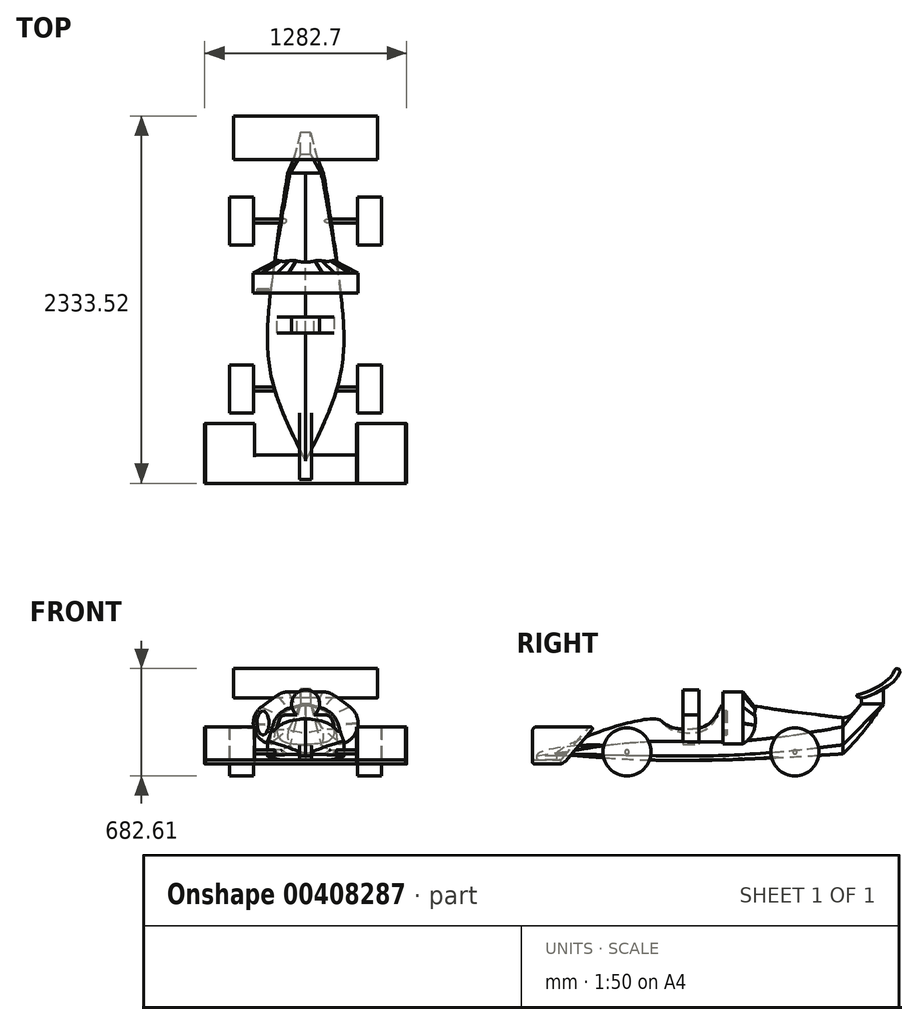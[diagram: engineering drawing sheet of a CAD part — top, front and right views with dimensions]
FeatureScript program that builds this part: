
annotation { "Feature Type Name" : "Feature", "Feature Type Description" : "" }
export const myFeature = defineFeature(function(context is Context, id is Id, definition is map)
    precondition{}
    {
        {
            var Q0;
            Q0=qCreatedBy(makeId("Right.planeOp"),FACE);
            var sketch = newSketch(context, id + "F0", { "sketchPlane" : qUnion([Q0])});
            skLineSegment(sketch, "E0", {"start": v(0, 0) * mm, "end": v(1066.8, 0) * mm, "construction": true});
            skLineSegment(sketch, "E1", {"start": v(0, 0) * mm, "end": v(-1066.8, 0) * mm, "construction": true});
            skLineSegment(sketch, "E2", {"start": v(0, 0) * mm, "end": v(0, 762) * mm, "construction": true});
            skSolve(sketch);
        }
        {
            var Q0;
            Q0=qCreatedBy(makeId("Front.planeOp"),FACE);
            cPlane(context, id + "F1", {"entities" : qUnion([Q0]), "cplaneType" : CPlaneType.OFFSET, "offset" : 1066.8 * mm, "width" : 152.4 * mm, "height" : 152.4 * mm});
        }
        {
            var Q0;
            Q0=qCreatedBy(makeId("Front.planeOp"),FACE);
            cPlane(context, id + "F2", {"entities" : qUnion([Q0]), "cplaneType" : CPlaneType.OFFSET, "offset" : 762 * mm, "oppositeDirection" : true, "width" : 152.4 * mm, "height" : 152.4 * mm});
        }
        {
            var Q0;
            Q0=qCreatedBy(id+"F1.planeOp",FACE);
            var sketch = newSketch(context, id + "F3", { "sketchPlane" : qUnion([Q0])});
            skLineSegment(sketch, "E3", {"start": v(0, 0) * mm, "end": v(0, 88.9) * mm, "construction": true});
            skPoint(sketch, "E4", {"position": v(0, 88.9) * mm});
            skSolve(sketch);
        }
        {
            var Q0;
            Q0=qCreatedBy(makeId("Front.planeOp"),FACE);
            cPlane(context, id + "F4", {"entities" : qUnion([Q0]), "cplaneType" : CPlaneType.OFFSET, "offset" : 508 * mm, "width" : 152.4 * mm, "height" : 152.4 * mm});
        }
        {
            var Q0;
            Q0=qCreatedBy(id+"F4.planeOp",FACE);
            var sketch = newSketch(context, id + "F5", { "sketchPlane" : qUnion([Q0])});
            skLineSegment(sketch, "E5", {"start": v(0, 0) * mm, "end": v(0, 304.8) * mm, "construction": true});
            skFitSpline(sketch, "E6", {"points": [v(0, 304.8) * mm, v(132.6, 270.36) * mm, v(222.86, 165.59) * mm], "startDerivative": vector(287.19, -34.12) * mm, "endDerivative": vector(158.63, -244.14) * mm});
            skLineSegment(sketch, "E7", {"start": v(222.86, 165.59) * mm, "end": v(222.86, 78.54) * mm});
            skFitSpline(sketch, "E8", {"points": [v(222.86, 78.54) * mm, v(150.32, 59.2) * mm, v(0, 51.14) * mm], "startDerivative": vector(-158.44, -53.56) * mm, "endDerivative": vector(-280.28, -4.09) * mm});
            skFitSpline(sketch, "E9.MirrorCS", {"points": [v(0, 304.8) * mm, v(-132.6, 270.36) * mm, v(-222.86, 165.59) * mm], "startDerivative": vector(-287.19, -34.12) * mm, "endDerivative": vector(-158.63, -244.14) * mm});
            skLineSegment(sketch, "E10.MirrorCS", {"start": v(-222.86, 165.59) * mm, "end": v(-222.86, 78.54) * mm});
            skFitSpline(sketch, "E11.MirrorCS", {"points": [v(-222.86, 78.54) * mm, v(-150.32, 59.2) * mm, v(0, 51.14) * mm], "startDerivative": vector(158.44, -53.56) * mm, "endDerivative": vector(280.28, -4.09) * mm});
            skSolve(sketch);
        }
        {
            var Q0;
            Q0=qCreatedBy(makeId("Front.planeOp"),FACE);
            var sketch = newSketch(context, id + "F6", { "sketchPlane" : qUnion([Q0])});
            skFitSpline(sketch, "E12.0", {"points": [v(-222.86, 78.54) * mm, v(-201, 71.16) * mm, v(-148.18, 53.3) * mm, v(-54.76, 51.94) * mm, v(0, 51.14) * mm]});
            skPoint(sketch, "E13.0", {"position": v(112.83, 54.96) * mm});
            skLineSegment(sketch, "E14.0", {"start": v(222.86, 165.59) * mm, "end": v(222.86, 78.54) * mm});
            skLineSegment(sketch, "E15.0", {"start": v(-222.86, 165.59) * mm, "end": v(-222.86, 78.54) * mm});
            skFitSpline(sketch, "E16", {"points": [v(-222.86, 165.59) * mm, v(-211.16, 257.47) * mm, v(-154.74, 352.57) * mm, v(-25.8, 402.54) * mm, v(0, 404.15) * mm], "startDerivative": vector(24.48, 349.4) * mm, "endDerivative": vector(143.3, -4.49) * mm});
            skFitSpline(sketch, "E17.MirrorCS", {"points": [v(222.86, 165.59) * mm, v(211.16, 257.47) * mm, v(154.74, 352.57) * mm, v(25.8, 402.54) * mm, v(0, 404.15) * mm], "startDerivative": vector(-24.48, 349.4) * mm, "endDerivative": vector(-143.3, -4.49) * mm});
            skFitSpline(sketch, "E18.MirrorCS", {"points": [v(222.86, 78.54) * mm, v(201, 71.16) * mm, v(148.18, 53.3) * mm, v(54.76, 51.94) * mm, v(0, 51.14) * mm]});
            skSolve(sketch);
        }
        {
            var Q0;
            Q0=qCreatedBy(id+"F2.planeOp",FACE);
            var sketch = newSketch(context, id + "F7", { "sketchPlane" : qUnion([Q0])});
            skLineSegment(sketch, "E19", {"start": v(0, 0) * mm, "end": v(0, 203.2) * mm, "construction": true});
            skCircle(sketch, "E20", {"center": v(0, 203.2) * mm, "radius": 114.3 * mm});
            skSolve(sketch);
        }
        {
            var Q0;
            Q0=qCreatedBy(makeId("Right.planeOp"),FACE);
            var sketch = newSketch(context, id + "F8", { "sketchPlane" : qUnion([Q0])});
            skPoint(sketch, "E21.0", {"position": v(-1066.8, 88.9) * mm});
            skFitSpline(sketch, "E22.0", {"points": [v(-508, 304.8) * mm, v(-508, 299.13) * mm, v(-508, 287.76) * mm, v(-508, 206.38) * mm, v(-508, 165.59) * mm]});
            skPoint(sketch, "E23.0", {"position": v(-508, 51.14) * mm});
            skPoint(sketch, "E24.0", {"position": v(0, 404.15) * mm});
            skPoint(sketch, "E25.0", {"position": v(0, 54.96) * mm});
            skLineSegment(sketch, "E26.0", {"start": v(762, 88.9) * mm, "end": v(762, 317.5) * mm});
            skFitSpline(sketch, "E27", {"points": [v(-1066.8, 88.9) * mm, v(-974.26, 150.13) * mm, v(-703.34, 256.94) * mm, v(-508, 304.8) * mm, v(-401.17, 304.8) * mm, v(-336.04, 249.12) * mm, v(-91.17, 254.33) * mm, v(0, 404.15) * mm, v(138.06, 404.15) * mm, v(401.17, 361.13) * mm, v(440.24, 355.92) * mm, v(762, 317.5) * mm], "startDerivative": vector(1027.27, 794.62) * mm, "endDerivative": vector(3267.51, -388.12) * mm});
            skFitSpline(sketch, "E28", {"points": [v(-1066.8, 88.9) * mm, v(-807.54, 51.14) * mm, v(-508, 51.14) * mm, v(0, 54.96) * mm, v(500.16, 54.96) * mm, v(762, 88.9) * mm], "startDerivative": vector(1511.97, -275.41) * mm, "endDerivative": vector(1399.72, 243.02) * mm});
            skSolve(sketch);
        }
        {
            var Q0;
            Q0=sQuery(id+"F8.wireOp",VERTEX,"E21.0");
            var Q1;
            Q1=makeQuery(id+"F5.imprint","IMPRINT",FACE,{"disambiguationData":[TD([[makeQuery(id+"F5.imprint","IMPRINT",EDGE,{"derivedFrom":sQuery(id+"F5.wireOp",EDGE,"E6")}),-1.0]])]});
            var Q2;
            Q2=makeQuery(id+"F6.imprint","IMPRINT",FACE,{"disambiguationData":[TD([[makeQuery(id+"F6.imprint","IMPRINT",EDGE,{"derivedFrom":sQuery(id+"F6.wireOp",EDGE,"E12.0")}),1.0]])]});
            var Q3;
            Q3=makeQuery(id+"F7.imprint","IMPRINT",FACE,{"disambiguationData":[TD([[makeQuery(id+"F7.imprint","IMPRINT",EDGE,{"derivedFrom":sQuery(id+"F7.wireOp",EDGE,"E20")}),1.0]])]});
            var Q4;
            Q4=sQuery(id+"F8.wireOp",EDGE,"E27");
            loft(context, id + "F9", {"addGuides" : true, "sheetProfilesArray" : [{ "sheetProfileEntities" : qUnion([Q0]) }, { "sheetProfileEntities" : qUnion([Q1]) }, { "sheetProfileEntities" : qUnion([Q2]) }, { "sheetProfileEntities" : qUnion([Q3]) }], "guidesArray" : [{ "guideEntities" : qUnion([Q4]), "guideDerivativeType" : LoftGuideDerivativeType.DEFAULT, "guideDerivativeMagnitude" : 1 }]});
        }
        {
            var Q0;
            Q0=qCreatedBy(makeId("Right.planeOp"),FACE);
            cPlane(context, id + "F10", {"entities" : qUnion([Q0]), "cplaneType" : CPlaneType.OFFSET, "offset" : 330.2 * mm, "width" : 152.4 * mm, "height" : 152.4 * mm});
        }
        {
            var Q0;
            Q0=qCreatedBy(id+"F10.planeOp",FACE);
            var sketch = newSketch(context, id + "F11", { "sketchPlane" : qUnion([Q0])});
            skLineSegment(sketch, "E29", {"start": v(0, 0) * mm, "end": v(-609.6, 0) * mm, "construction": true});
            skLineSegment(sketch, "E30", {"start": v(-609.6, 0) * mm, "end": v(-609.6, 101.6) * mm, "construction": true});
            skLineSegment(sketch, "E31", {"start": v(0, 0) * mm, "end": v(457.2, 0) * mm, "construction": true});
            skLineSegment(sketch, "E32", {"start": v(457.2, 0) * mm, "end": v(457.2, 101.6) * mm, "construction": true});
            skCircle(sketch, "E33", {"center": v(-609.6, 101.6) * mm, "radius": 152.4 * mm});
            skCircle(sketch, "E34", {"center": v(457.2, 101.6) * mm, "radius": 152.4 * mm});
            skSolve(sketch);
        }
        {
            var Q0;
            Q0=makeQuery(id+"F11.imprint","IMPRINT",FACE,{"disambiguationData":[TD([[makeQuery(id+"F11.imprint","IMPRINT",EDGE,{"derivedFrom":sQuery(id+"F11.wireOp",EDGE,"E33")}),1.0]])]});
            var Q1;
            Q1=makeQuery(id+"F11.imprint","IMPRINT",FACE,{"disambiguationData":[TD([[makeQuery(id+"F11.imprint","IMPRINT",EDGE,{"derivedFrom":sQuery(id+"F11.wireOp",EDGE,"E34")}),1.0]])]});
            extrude(context, id + "F12", {"entities" : qUnion([Q0, Q1]), "depth" : 152.4 * mm});
        }
        {
            var Q0;
            Q0=makeQuery(id+"F12.opExtrude","CAP_FACE",FACE,{"disambiguationData":[OSD([sQuery(id+"F11.wireOp",EDGE,"E33")])],"isStart":true});
            var sketch = newSketch(context, id + "F13", { "sketchPlane" : qUnion([Q0])});
            skCircle(sketch, "E35", {"center": v(609.6, 101.6) * mm, "radius": 12.7 * mm});
            skSolve(sketch);
        }
        {
            var Q0;
            Q0=makeQuery(id+"F13.imprint","IMPRINT",FACE,{"disambiguationData":[TD([[makeQuery(id+"F13.imprint","IMPRINT",EDGE,{"derivedFrom":sQuery(id+"F13.wireOp",EDGE,"E35")}),1.0]])]});
            extrude(context, id + "F14", {"entities" : qUnion([Q0]), "endBound" : BoundingType.UP_TO_NEXT, "depth" : 25.4 * mm});
        }
        {
            var Q0;
            Q0=makeQuery(id+"F12.opExtrude","CAP_FACE",FACE,{"disambiguationData":[OSD([sQuery(id+"F11.wireOp",EDGE,"E34")])],"isStart":true});
            var sketch = newSketch(context, id + "F15", { "sketchPlane" : qUnion([Q0])});
            skCircle(sketch, "E36", {"center": v(-457.2, 101.6) * mm, "radius": 12.7 * mm});
            skSolve(sketch);
        }
        {
            var Q0;
            Q0=makeQuery(id+"F15.imprint","IMPRINT",FACE,{"disambiguationData":[TD([[makeQuery(id+"F15.imprint","IMPRINT",EDGE,{"derivedFrom":sQuery(id+"F15.wireOp",EDGE,"E36")}),1.0]])]});
            extrude(context, id + "F16", {"entities" : qUnion([Q0]), "endBound" : BoundingType.UP_TO_NEXT, "depth" : 25.4 * mm});
        }
        {
            var Q0;
            Q0=qCreatedBy(makeId("Right.planeOp"),FACE);
            var sketch = newSketch(context, id + "F17", { "sketchPlane" : qUnion([Q0])});
            skFitSpline(sketch, "E37", {"points": [v(873.59, 445.04) * mm, v(963.54, 473.71) * mm, v(1092.94, 556.82) * mm, v(1122.28, 622.83) * mm, v(1097.34, 630.16) * mm, v(1081.2, 597.9) * mm, v(1017, 537) * mm, v(949.39, 498.44) * mm, v(889.96, 474.72) * mm, v(847.68, 458.19) * mm, v(873.59, 445.04) * mm]});
            skSolve(sketch);
        }
        {
            var Q0;
            Q0=makeQuery(id+"F17.imprint","IMPRINT",FACE,{"disambiguationData":[TD([[makeQuery(id+"F17.imprint","IMPRINT",EDGE,{"derivedFrom":sQuery(id+"F17.wireOp",EDGE,"E37")}),1.0]])]});
            extrude(context, id + "F18", {"entities" : qUnion([Q0]), "endBound" : BoundingType.SYMMETRIC, "depth" : 914.4 * mm});
        }
        {
            var Q0;
            Q0=makeQuery(id+"F18.opExtrude","CAP_FACE",FACE,{"disambiguationData":[OSD([sQuery(id+"F17.wireOp",EDGE,"E37")])],"isStart":false});
            cPlane(context, id + "F19", {"entities" : qUnion([Q0]), "cplaneType" : CPlaneType.OFFSET, "offset" : 177.8 * mm, "width" : 152.4 * mm, "height" : 152.4 * mm});
        }
        {
            var Q0;
            Q0=qCreatedBy(id+"F19.planeOp",FACE);
            var sketch = newSketch(context, id + "F20", { "sketchPlane" : qUnion([Q0])});
            skArc(sketch, "E38", {"start": v(-1196.29, 50.01) * mm, "mid": v(-1208.99, 37.31) * mm, "end": v(-1196.29, 24.61) * mm});
            skLineSegment(sketch, "E39", {"start": v(-1196.29, 50.01) * mm, "end": v(-1039.81, 50.01) * mm});
            skLineSegment(sketch, "E40", {"start": v(-1020.5, 58.9) * mm, "end": v(-851.65, 256.45) * mm});
            skPoint(sketch, "E41.visualSharp", {"position": v(-1028.11, 50.01) * mm});
            skArc(sketch, "E41.filletArc", {"start": v(-1039.81, 50.01) * mm, "mid": v(-1029.18, 52.34) * mm, "end": v(-1020.5, 58.9) * mm});
            skLineSegment(sketch, "E42.0", {"start": v(-1001.2, 42.4) * mm, "end": v(-832.34, 239.94) * mm});
            skArc(sketch, "E42.1", {"start": v(-1039.81, 24.61) * mm, "mid": v(-1018.56, 29.28) * mm, "end": v(-1001.2, 42.4) * mm});
            skLineSegment(sketch, "E42.2", {"start": v(-1196.29, 24.61) * mm, "end": v(-1039.81, 24.61) * mm});
            skArc(sketch, "E43", {"start": v(-851.65, 256.45) * mm, "mid": v(-833.74, 257.85) * mm, "end": v(-832.34, 239.94) * mm});
            skSolve(sketch);
        }
        {
            var Q0;
            Q0 = qSketchRegion(id + "F20", true);
            extrude(context, id + "F21", {"entities" : qUnion([Q0]), "oppositeDirection" : true, "depth" : 304.8 * mm});
        }
        {
            var Q0;
            Q0=makeQuery(id+"F21.opExtrude","CAP_FACE",FACE,{"disambiguationData":[OSD([sQuery(id+"F20.wireOp",EDGE,"E38"),sQuery(id+"F20.wireOp",EDGE,"E39"),sQuery(id+"F20.wireOp",EDGE,"E40"),sQuery(id+"F20.wireOp",EDGE,"E41.filletArc"),sQuery(id+"F20.wireOp",EDGE,"E42.0"),sQuery(id+"F20.wireOp",EDGE,"E42.1"),sQuery(id+"F20.wireOp",EDGE,"E42.2"),sQuery(id+"F20.wireOp",EDGE,"E43")])],"isStart":false});
            var sketch = newSketch(context, id + "F22", { "sketchPlane" : qUnion([Q0])});
            skArc(sketch, "E44.0", {"start": v(1196.29, 50.01) * mm, "mid": v(1208.99, 37.31) * mm, "end": v(1196.29, 24.61) * mm});
            skLineSegment(sketch, "E45.0", {"start": v(1196.29, 50.01) * mm, "end": v(1039.81, 50.01) * mm});
            skLineSegment(sketch, "E46.0", {"start": v(1196.29, 24.61) * mm, "end": v(1039.81, 24.61) * mm});
            skArc(sketch, "E47", {"start": v(1039.81, 50.01) * mm, "mid": v(1027.11, 37.31) * mm, "end": v(1039.81, 24.61) * mm});
            skSolve(sketch);
        }
        {
            var Q0;
            Q0=makeQuery(id+"F22.imprint","IMPRINT",FACE,{"disambiguationData":[TD([[makeQuery(id+"F22.imprint","IMPRINT",EDGE,{"derivedFrom":sQuery(id+"F22.wireOp",EDGE,"E44.0")}),-1.0]])]});
            var Q1;
            Q1=qCreatedBy(makeId("Right.planeOp"),FACE);
            extrude(context, id + "F23", {"entities" : qUnion([Q0]), "operationType" : NewBodyOperationType.ADD, "endBound" : BoundingType.UP_TO_SURFACE, "endBoundEntityFace" : qUnion([Q1]), "depth" : 25.4 * mm});
        }
        {
            var Q0;
            Q0=makeQuery(id+"F21.opExtrude","SWEPT_BODY",BODY,{"disambiguationData":[OSD([sQuery(id+"F20.wireOp",EDGE,"E38"),sQuery(id+"F20.wireOp",EDGE,"E39"),sQuery(id+"F20.wireOp",EDGE,"E40"),sQuery(id+"F20.wireOp",EDGE,"E41.filletArc"),sQuery(id+"F20.wireOp",EDGE,"E42.0"),sQuery(id+"F20.wireOp",EDGE,"E42.1"),sQuery(id+"F20.wireOp",EDGE,"E42.2"),sQuery(id+"F20.wireOp",EDGE,"E43")])]});
            var Q1;
            Q1=qCreatedBy(makeId("Right.planeOp"),FACE);
            mirror(context, id + "F24", {"operationType" : NewBodyOperationType.ADD, "entities" : qUnion([Q0]), "mirrorPlane" : qUnion([Q1])});
        }
        {
            var Q0;
            Q0=makeQuery(id+"F21.opExtrude","CAP_FACE",FACE,{"disambiguationData":[OSD([sQuery(id+"F20.wireOp",EDGE,"E38"),sQuery(id+"F20.wireOp",EDGE,"E39"),sQuery(id+"F20.wireOp",EDGE,"E40"),sQuery(id+"F20.wireOp",EDGE,"E41.filletArc"),sQuery(id+"F20.wireOp",EDGE,"E42.0"),sQuery(id+"F20.wireOp",EDGE,"E42.1"),sQuery(id+"F20.wireOp",EDGE,"E42.2"),sQuery(id+"F20.wireOp",EDGE,"E43")])],"isStart":true});
            var sketch = newSketch(context, id + "F25", { "sketchPlane" : qUnion([Q0])});
            skArc(sketch, "E48.0", {"start": v(-851.65, 256.45) * mm, "mid": v(-833.74, 257.85) * mm, "end": v(-832.34, 239.94) * mm, "construction": true});
            skArc(sketch, "E49.0", {"start": v(-1196.29, 50.01) * mm, "mid": v(-1208.99, 37.31) * mm, "end": v(-1196.29, 24.61) * mm, "construction": true});
            skLineSegment(sketch, "E50", {"start": v(-842, 248.2) * mm, "end": v(-842, 260.9) * mm, "construction": true});
            skLineSegment(sketch, "E51", {"start": v(-842, 260.9) * mm, "end": v(-1183.59, 260.9) * mm});
            skPoint(sketch, "E51.endSnap0", {"position": v(-1208.99, 37.31) * mm});
            skLineSegment(sketch, "E52", {"start": v(-1208.99, 235.5) * mm, "end": v(-1208.99, 37.31) * mm});
            skPoint(sketch, "E53.visualSharp", {"position": v(-1208.99, 260.9) * mm});
            skArc(sketch, "E53.filletArc", {"start": v(-1183.59, 260.9) * mm, "mid": v(-1201.55, 253.45) * mm, "end": v(-1208.99, 235.5) * mm});
            skLineSegment(sketch, "E54.0", {"start": v(-1196.29, 24.61) * mm, "end": v(-1039.81, 24.61) * mm});
            skArc(sketch, "E55.0", {"start": v(-1039.81, 24.61) * mm, "mid": v(-1018.56, 29.28) * mm, "end": v(-1001.2, 42.4) * mm});
            skLineSegment(sketch, "E56.0", {"start": v(-1001.2, 42.4) * mm, "end": v(-832.34, 239.94) * mm});
            skSolve(sketch);
        }
        {
            var Q0;
            {var subQ2=sQuery(id+"F25.wireOp",EDGE,"E54.0");Q0=makeQuery(id+"F25.imprint","IMPRINT",FACE,{"disambiguationData":[TD([[makeQuery(id+"F25.imprint","IMPRINT",EDGE,{"derivedFrom":subQ2}),1.0]])]});}
            var Q1;
            {var subQ4=sQuery(id+"F25.wireOp",EDGE,"E51");Q1=makeQuery(id+"F25.imprint","IMPRINT",FACE,{"disambiguationData":[TD([[makeQuery(id+"F25.imprint","IMPRINT",EDGE,{"derivedFrom":subQ4}),1.0]])]});}
            extrude(context, id + "F26", {"entities" : qUnion([Q0, Q1]), "operationType" : NewBodyOperationType.ADD, "depth" : 6.35 * mm});
        }
        {
            var Q0;
            Q0=makeQuery(id+"F24.opPattern","COPY",FACE,{"derivedFrom":makeQuery(id+"F21.opExtrude","CAP_FACE",FACE,{"disambiguationData":[OSD([sQuery(id+"F20.wireOp",EDGE,"E38"),sQuery(id+"F20.wireOp",EDGE,"E39"),sQuery(id+"F20.wireOp",EDGE,"E40"),sQuery(id+"F20.wireOp",EDGE,"E41.filletArc"),sQuery(id+"F20.wireOp",EDGE,"E42.0"),sQuery(id+"F20.wireOp",EDGE,"E42.1"),sQuery(id+"F20.wireOp",EDGE,"E42.2"),sQuery(id+"F20.wireOp",EDGE,"E43")])],"isStart":true}),"instanceName":"1"});
            var sketch = newSketch(context, id + "F27", { "sketchPlane" : qUnion([Q0])});
            skArc(sketch, "E57.0.0", {"start": v(842, 260.9) * mm, "mid": v(847.31, 259.73) * mm, "end": v(851.65, 256.45) * mm});
            skLineSegment(sketch, "E57.0.1", {"start": v(851.65, 256.45) * mm, "end": v(1020.5, 58.9) * mm});
            skArc(sketch, "E57.0.2", {"start": v(1020.5, 58.9) * mm, "mid": v(1029.18, 52.34) * mm, "end": v(1039.81, 50.01) * mm});
            skLineSegment(sketch, "E57.0.3", {"start": v(1039.81, 50.01) * mm, "end": v(1196.29, 50.01) * mm});
            skArc(sketch, "E57.0.4", {"start": v(1196.29, 50.01) * mm, "mid": v(1205.27, 46.3) * mm, "end": v(1208.99, 37.31) * mm});
            skLineSegment(sketch, "E57.0.5", {"start": v(1208.99, 37.31) * mm, "end": v(1208.99, 235.5) * mm});
            skArc(sketch, "E57.0.6", {"start": v(1208.99, 235.5) * mm, "mid": v(1201.55, 253.45) * mm, "end": v(1183.59, 260.9) * mm});
            skLineSegment(sketch, "E57.0.7", {"start": v(1183.59, 260.9) * mm, "end": v(842, 260.9) * mm});
            skSolve(sketch);
        }
        {
            var Q0;
            Q0=makeQuery(id+"F27.imprint","IMPRINT",FACE,{"disambiguationData":[TD([[makeQuery(id+"F27.imprint","IMPRINT",EDGE,{"derivedFrom":sQuery(id+"F27.wireOp",EDGE,"E57.0.0")}),-1.0]])]});
            var Q1;
            {var subQ2=sQuery(id+"F27.wireOp",EDGE,"E57.0.0");Q1=makeQuery(id+"F27.imprint","IMPRINT",FACE,{"disambiguationData":[TD([[makeQuery(id+"F27.imprint","IMPRINT",EDGE,{"derivedFrom":subQ2}),1.0]])]});}
            extrude(context, id + "F28", {"entities" : qUnion([Q0, Q1]), "operationType" : NewBodyOperationType.ADD, "depth" : 6.35 * mm});
        }
        {
            var Q0;
            Q0=makeQuery(id+"F21.opExtrude","CAP_FACE",FACE,{"disambiguationData":[OSD([sQuery(id+"F20.wireOp",EDGE,"E38"),sQuery(id+"F20.wireOp",EDGE,"E39"),sQuery(id+"F20.wireOp",EDGE,"E40"),sQuery(id+"F20.wireOp",EDGE,"E41.filletArc"),sQuery(id+"F20.wireOp",EDGE,"E42.0"),sQuery(id+"F20.wireOp",EDGE,"E42.1"),sQuery(id+"F20.wireOp",EDGE,"E42.2"),sQuery(id+"F20.wireOp",EDGE,"E43")])],"isStart":false});
            var sketch = newSketch(context, id + "F29", { "sketchPlane" : qUnion([Q0])});
            skArc(sketch, "E58.0.0", {"start": v(842, 260.9) * mm, "mid": v(847.31, 259.73) * mm, "end": v(851.65, 256.45) * mm});
            skLineSegment(sketch, "E58.0.1", {"start": v(851.65, 256.45) * mm, "end": v(1020.5, 58.9) * mm});
            skArc(sketch, "E58.0.2", {"start": v(1020.5, 58.9) * mm, "mid": v(1029.18, 52.34) * mm, "end": v(1039.81, 50.01) * mm});
            skLineSegment(sketch, "E58.0.3", {"start": v(1039.81, 50.01) * mm, "end": v(1196.29, 50.01) * mm});
            skArc(sketch, "E58.0.4", {"start": v(1196.29, 50.01) * mm, "mid": v(1205.27, 46.3) * mm, "end": v(1208.99, 37.31) * mm});
            skLineSegment(sketch, "E58.0.5", {"start": v(1208.99, 37.31) * mm, "end": v(1208.99, 235.5) * mm});
            skArc(sketch, "E58.0.6", {"start": v(1208.99, 235.5) * mm, "mid": v(1201.55, 253.45) * mm, "end": v(1183.59, 260.9) * mm});
            skLineSegment(sketch, "E58.0.7", {"start": v(1183.59, 260.9) * mm, "end": v(842, 260.9) * mm});
            skSolve(sketch);
        }
        {
            var Q0;
            Q0=makeQuery(id+"F29.imprint","IMPRINT",FACE,{"disambiguationData":[TD([[makeQuery(id+"F29.imprint","IMPRINT",EDGE,{"derivedFrom":sQuery(id+"F29.wireOp",EDGE,"E58.0.0")}),-1.0]])]});
            var Q1;
            {var subQ1=sQuery(id+"F29.wireOp",EDGE,"E58.0.0");Q1=makeQuery(id+"F29.imprint","IMPRINT",FACE,{"disambiguationData":[TD([[makeQuery(id+"F29.imprint","IMPRINT",EDGE,{"derivedFrom":subQ1}),1.0]])]});}
            extrude(context, id + "F30", {"entities" : qUnion([Q0, Q1]), "operationType" : NewBodyOperationType.ADD, "depth" : 6.35 * mm});
        }
        {
            var Q0;
            Q0=makeQuery(id+"F24.opPattern","COPY",FACE,{"derivedFrom":makeQuery(id+"F21.opExtrude","CAP_FACE",FACE,{"disambiguationData":[OSD([sQuery(id+"F20.wireOp",EDGE,"E38"),sQuery(id+"F20.wireOp",EDGE,"E39"),sQuery(id+"F20.wireOp",EDGE,"E40"),sQuery(id+"F20.wireOp",EDGE,"E41.filletArc"),sQuery(id+"F20.wireOp",EDGE,"E42.0"),sQuery(id+"F20.wireOp",EDGE,"E42.1"),sQuery(id+"F20.wireOp",EDGE,"E42.2"),sQuery(id+"F20.wireOp",EDGE,"E43")])],"isStart":false}),"instanceName":"1"});
            var sketch = newSketch(context, id + "F31", { "sketchPlane" : qUnion([Q0])});
            skArc(sketch, "E59.0.0", {"start": v(-1208.99, 37.31) * mm, "mid": v(-1205.27, 46.3) * mm, "end": v(-1196.29, 50.01) * mm});
            skLineSegment(sketch, "E59.0.1", {"start": v(-1196.29, 50.01) * mm, "end": v(-1039.81, 50.01) * mm});
            skArc(sketch, "E59.0.2", {"start": v(-1039.81, 50.01) * mm, "mid": v(-1029.18, 52.34) * mm, "end": v(-1020.5, 58.9) * mm});
            skLineSegment(sketch, "E59.0.3", {"start": v(-1020.5, 58.9) * mm, "end": v(-851.65, 256.45) * mm});
            skArc(sketch, "E59.0.4", {"start": v(-851.65, 256.45) * mm, "mid": v(-847.31, 259.73) * mm, "end": v(-842, 260.9) * mm});
            skLineSegment(sketch, "E59.0.5", {"start": v(-842, 260.9) * mm, "end": v(-1183.59, 260.9) * mm});
            skArc(sketch, "E59.0.6", {"start": v(-1183.59, 260.9) * mm, "mid": v(-1201.55, 253.45) * mm, "end": v(-1208.99, 235.5) * mm});
            skLineSegment(sketch, "E59.0.7", {"start": v(-1208.99, 235.5) * mm, "end": v(-1208.99, 37.31) * mm});
            skSolve(sketch);
        }
        {
            var Q0;
            Q0=makeQuery(id+"F31.imprint","IMPRINT",FACE,{"disambiguationData":[TD([[makeQuery(id+"F31.imprint","IMPRINT",EDGE,{"derivedFrom":sQuery(id+"F31.wireOp",EDGE,"E59.0.0")}),1.0]])]});
            var Q1;
            Q1=makeQuery(id+"F31.imprint","IMPRINT",FACE,{"disambiguationData":[TD([[makeQuery(id+"F31.imprint","IMPRINT",EDGE,{"derivedFrom":sQuery(id+"F31.wireOp",EDGE,"E59.0.2")}),-1.0]])]});
            extrude(context, id + "F32", {"entities" : qUnion([Q0, Q1]), "operationType" : NewBodyOperationType.ADD, "depth" : 6.35 * mm});
        }
        {
            var Q0;
            Q0=qCreatedBy(makeId("Front.planeOp"),FACE);
            cPlane(context, id + "F33", {"entities" : qUnion([Q0]), "cplaneType" : CPlaneType.OFFSET, "offset" : 152.4 * mm, "width" : 152.4 * mm, "height" : 152.4 * mm});
        }
        {
            var Q0;
            Q0=qCreatedBy(id+"F33.planeOp",FACE);
            var sketch = newSketch(context, id + "F34", { "sketchPlane" : qUnion([Q0])});
            skLineSegment(sketch, "E60", {"start": v(0, 0) * mm, "end": v(0, 406.4) * mm, "construction": true});
            skCircle(sketch, "E61", {"center": v(0, 406.4) * mm, "radius": 88.9 * mm});
            skFitSpline(sketch, "E62", {"points": [v(-53.89, 335.7) * mm, v(-130.83, 334.95) * mm, v(-160.46, 317.85) * mm, v(-171.86, 194.75) * mm, v(0, 149.16) * mm], "startDerivative": vector(-386.02, 8.43) * mm, "endDerivative": vector(651.34, -15.56) * mm});
            skFitSpline(sketch, "E63.MirrorCS", {"points": [v(53.89, 335.7) * mm, v(130.83, 334.95) * mm, v(160.46, 317.85) * mm, v(171.86, 194.75) * mm, v(0, 149.16) * mm], "startDerivative": vector(386.02, 8.43) * mm, "endDerivative": vector(-651.34, -15.56) * mm});
            skSolve(sketch);
        }
        {
            var Q0;
            {var subQ0=sQuery(id+"F34.wireOp",EDGE,"E62");Q0=makeQuery(id+"F34.imprint","IMPRINT",FACE,{"disambiguationData":[TD([[makeQuery(id+"F34.imprint","IMPRINT",EDGE,{"derivedFrom":subQ0}),1.0]])]});}
            var Q1;
            {var subQ0=sQuery(id+"F34.wireOp",EDGE,"E61");var subQ1=makeQuery(id+"F34.imprint","INTERSECT",VERTEX,{"derivedFrom":[subQ0,sQuery(id+"F34.wireOp",EDGE,"E62")]});Q1=makeQuery(id+"F34.imprint","IMPRINT",FACE,{"disambiguationData":[TD([[makeQuery(id+"F34.imprint","IMPRINT",EDGE,{"disambiguationData":[TD([[subQ1,-1.0]])],"derivedFrom":subQ0}),1.0]])]});}
            extrude(context, id + "F35", {"entities" : qUnion([Q0, Q1]), "depth" : 101.6 * mm});
        }
        {
            var Q0;
            {var subQ0=sQuery(id+"F22.wireOp",EDGE,"E47");var subQ1=makeQuery(id+"F23.opExtrude","SWEPT_FACE",FACE,{"disambiguationData":[OSD([subQ0])]});var subQ15=sQuery(id+"F20.wireOp",EDGE,"E39");var subQ16=makeQuery(id+"F23.boolean.opBoolean","MERGE",FACE,{"derivedFrom":[makeQuery(id+"F21.opExtrude","SWEPT_FACE",FACE,{"disambiguationData":[OSD([subQ15])]}),makeQuery(id+"F23.opExtrude","SWEPT_FACE",FACE,{"disambiguationData":[OSD([sQuery(id+"F22.wireOp",EDGE,"E45.0")])]})]});Q0=makeQuery(id+"F32.boolean.opBoolean","SPLIT",FACE,{"disambiguationData":[TD([subQ1])],"derivedFrom":makeQuery(id+"F30.boolean.opBoolean","SPLIT",FACE,{"disambiguationData":[TD([subQ1])],"derivedFrom":makeQuery(id+"F24.boolean.opBoolean","MERGE",FACE,{"derivedFrom":[subQ16,makeQuery(id+"F24.opPattern","COPY",FACE,{"derivedFrom":subQ16,"instanceName":"1"})]})})});}
            var sketch = newSketch(context, id + "F36", { "sketchPlane" : qUnion([Q0])});
            skLineSegment(sketch, "E64", {"start": v(0, -1196.29) * mm, "end": v(0, -1120.09) * mm, "construction": true});
            skPoint(sketch, "E64.endSnap0", {"position": v(0, -1196.29) * mm});
            skLineSegment(sketch, "E65.bottom", {"start": v(38.1, -1056.59) * mm, "end": v(-38.1, -1056.59) * mm});
            skLineSegment(sketch, "E65.top", {"start": v(38.1, -1183.59) * mm, "end": v(-38.1, -1183.59) * mm});
            skLineSegment(sketch, "E65.left", {"start": v(38.1, -1056.59) * mm, "end": v(38.1, -1183.59) * mm});
            skLineSegment(sketch, "E65.right", {"start": v(-38.1, -1056.59) * mm, "end": v(-38.1, -1183.59) * mm});
            skPoint(sketch, "E65.middle", {"position": v(0, -1120.09) * mm});
            skSolve(sketch);
        }
        {
            var Q0;
            Q0=makeQuery(id+"F36.imprint","IMPRINT",FACE,{"disambiguationData":[TD([[makeQuery(id+"F36.imprint","IMPRINT",EDGE,{"derivedFrom":sQuery(id+"F36.wireOp",EDGE,"E65.bottom")}),1.0]])]});
            extrude(context, id + "F37", {"entities" : qUnion([Q0]), "operationType" : NewBodyOperationType.ADD, "depth" : 25.4 * mm});
        }
        {
            var Q0;
            Q0=qCreatedBy(makeId("Front.planeOp"),FACE);
            cPlane(context, id + "F38", {"entities" : qUnion([Q0]), "cplaneType" : CPlaneType.OFFSET, "offset" : 762 * mm, "width" : 152.4 * mm, "height" : 152.4 * mm});
        }
        {
            var Q0;
            Q0=qCreatedBy(id+"F38.planeOp",FACE);
            var sketch = newSketch(context, id + "F39", { "sketchPlane" : qUnion([Q0])});
            skLineSegment(sketch, "E66", {"start": v(0, 0) * mm, "end": v(0, 118.06) * mm, "construction": true});
            skLineSegment(sketch, "E67.bottom", {"start": v(38.1, 143.46) * mm, "end": v(-38.1, 143.46) * mm});
            skLineSegment(sketch, "E67.top", {"start": v(38.1, 92.66) * mm, "end": v(-38.1, 92.66) * mm});
            skLineSegment(sketch, "E67.left", {"start": v(38.1, 143.46) * mm, "end": v(38.1, 92.66) * mm});
            skLineSegment(sketch, "E67.right", {"start": v(-38.1, 143.46) * mm, "end": v(-38.1, 92.66) * mm});
            skPoint(sketch, "E67.middle", {"position": v(0, 118.06) * mm});
            skSolve(sketch);
        }
        {
            var Q0;
            Q0=qCreatedBy(makeId("Right.planeOp"),FACE);
            var sketch = newSketch(context, id + "F40", { "sketchPlane" : qUnion([Q0])});
            skLineSegment(sketch, "E68.0", {"start": v(-1056.59, 75.41) * mm, "end": v(-1056.59, 50.01) * mm});
            skPoint(sketch, "E69.0", {"position": v(-1183.59, 75.41) * mm});
            skPoint(sketch, "E70.0", {"position": v(-762, 143.46) * mm});
            skPoint(sketch, "E71.0", {"position": v(-762, 92.66) * mm});
            skFitSpline(sketch, "E72", {"points": [v(-762, 143.46) * mm, v(-882.63, 143.46) * mm, v(-1158.41, 100.54) * mm, v(-1183.59, 75.41) * mm], "startDerivative": vector(-294.14, 14.74) * mm, "endDerivative": vector(-72.57, -146.11) * mm});
            skFitSpline(sketch, "E73", {"points": [v(-762, 92.66) * mm, v(-972.73, 92.66) * mm, v(-1056.59, 75.41) * mm], "startDerivative": vector(-384.64, 13.53) * mm, "endDerivative": vector(-190.18, -52.94) * mm});
            skSolve(sketch);
        }
        {
            var Q0;
            Q0=makeQuery(id+"F37.opExtrude","CAP_FACE",FACE,{"disambiguationData":[OSD([sQuery(id+"F36.wireOp",EDGE,"E65.bottom"),sQuery(id+"F36.wireOp",EDGE,"E65.top"),sQuery(id+"F36.wireOp",EDGE,"E65.left"),sQuery(id+"F36.wireOp",EDGE,"E65.right")])],"isStart":false});
            var Q1;
            Q1 = qSketchRegion(id + "F39", true);
            var Q2;
            Q2=sQuery(id+"F40.wireOp",EDGE,"E72");
            loft(context, id + "F41", {"addGuides" : true, "sheetProfilesArray" : [{ "sheetProfileEntities" : qUnion([Q0]) }, { "sheetProfileEntities" : qUnion([Q1]) }], "guidesArray" : [{ "guideEntities" : qUnion([Q2]), "guideDerivativeType" : LoftGuideDerivativeType.DEFAULT, "guideDerivativeMagnitude" : 1 }]});
        }
        {
            var Q0;
            Q0=makeQuery(id+"F14.opExtrude","SWEPT_BODY",BODY,{"disambiguationData":[OSD([sQuery(id+"F13.wireOp",EDGE,"E35")])]});
            var Q1;
            Q1=makeQuery(id+"F16.opExtrude","SWEPT_BODY",BODY,{"disambiguationData":[OSD([sQuery(id+"F15.wireOp",EDGE,"E36")])]});
            var Q2;
            Q2=makeQuery(id+"F12.opExtrude","SWEPT_BODY",BODY,{"disambiguationData":[OSD([sQuery(id+"F11.wireOp",EDGE,"E33")])]});
            var Q3;
            Q3=makeQuery(id+"F12.opExtrude","SWEPT_BODY",BODY,{"disambiguationData":[OSD([sQuery(id+"F11.wireOp",EDGE,"E34")])]});
            var Q4;
            Q4=qCreatedBy(makeId("Right.planeOp"),FACE);
            mirror(context, id + "F42", {"entities" : qUnion([Q0, Q1, Q2, Q3]), "mirrorPlane" : qUnion([Q4])});
        }
        {
            var Q0;
            Q0=qCreatedBy(makeId("Front.planeOp"),FACE);
            var sketch = newSketch(context, id + "F43", { "sketchPlane" : qUnion([Q0])});
            skLineSegment(sketch, "E74", {"start": v(0, 0) * mm, "end": v(0, 152.4) * mm, "construction": true});
            skLineSegment(sketch, "E75", {"start": v(0, 152.4) * mm, "end": v(205.42, 152.4) * mm});
            skLineSegment(sketch, "E76", {"start": v(332.42, 279.4) * mm, "end": v(332.42, 284.65) * mm});
            skLineSegment(sketch, "E77", {"start": v(280.44, 387.13) * mm, "end": v(182.77, 458.62) * mm});
            skLineSegment(sketch, "E78", {"start": v(107.76, 483.14) * mm, "end": v(0, 483.14) * mm});
            skPoint(sketch, "E79.visualSharp", {"position": v(149.27, 483.14) * mm});
            skArc(sketch, "E79.filletArc", {"start": v(182.77, 458.62) * mm, "mid": v(147.21, 476.85) * mm, "end": v(107.76, 483.14) * mm});
            skPoint(sketch, "E80.visualSharp", {"position": v(332.42, 349.08) * mm});
            skArc(sketch, "E80.filletArc", {"start": v(332.42, 284.65) * mm, "mid": v(318.68, 342.1) * mm, "end": v(280.44, 387.13) * mm});
            skPoint(sketch, "E81.visualSharp", {"position": v(332.42, 152.4) * mm});
            skArc(sketch, "E81.filletArc", {"start": v(205.42, 152.4) * mm, "mid": v(295.23, 189.6) * mm, "end": v(332.42, 279.4) * mm});
            skLineSegment(sketch, "E82.MirrorCS", {"start": v(-107.76, 483.14) * mm, "end": v(0, 483.14) * mm});
            skArc(sketch, "E83.MirrorCS", {"start": v(-182.77, 458.62) * mm, "mid": v(-147.21, 476.85) * mm, "end": v(-107.76, 483.14) * mm});
            skLineSegment(sketch, "E84.MirrorCS", {"start": v(-280.44, 387.13) * mm, "end": v(-182.77, 458.62) * mm});
            skArc(sketch, "E85.MirrorCS", {"start": v(-332.42, 284.65) * mm, "mid": v(-318.68, 342.1) * mm, "end": v(-280.44, 387.13) * mm});
            skArc(sketch, "E86.MirrorCS", {"start": v(-205.42, 152.4) * mm, "mid": v(-295.23, 189.6) * mm, "end": v(-332.42, 279.4) * mm});
            skLineSegment(sketch, "E87.MirrorCS", {"start": v(0, 152.4) * mm, "end": v(-205.42, 152.4) * mm});
            skLineSegment(sketch, "E88", {"start": v(-205.42, 152.4) * mm, "end": v(205.42, 152.4) * mm});
            skLineSegment(sketch, "E89", {"start": v(-332.42, 284.65) * mm, "end": v(-332.42, 279.4) * mm});
            skSolve(sketch);
        }
        {
            var Q0;
            Q0=makeQuery(id+"F43.imprint","IMPRINT",FACE,{"disambiguationData":[TD([[makeQuery(id+"F43.imprint","IMPRINT",EDGE,{"derivedFrom":sQuery(id+"F43.wireOp",EDGE,"E76")}),1.0]])]});
            extrude(context, id + "F44", {"entities" : qUnion([Q0]), "operationType" : NewBodyOperationType.ADD, "oppositeDirection" : true, "depth" : 127 * mm});
        }
        {
            var Q0;
            Q0=makeQuery(id+"F44.opExtrude","CAP_FACE",FACE,{"disambiguationData":[OSD([sQuery(id+"F43.wireOp",EDGE,"E76"),sQuery(id+"F43.wireOp",EDGE,"E77"),sQuery(id+"F43.wireOp",EDGE,"E78"),sQuery(id+"F43.wireOp",EDGE,"E79.filletArc"),sQuery(id+"F43.wireOp",EDGE,"E80.filletArc"),sQuery(id+"F43.wireOp",EDGE,"E81.filletArc"),sQuery(id+"F43.wireOp",EDGE,"E82.MirrorCS"),sQuery(id+"F43.wireOp",EDGE,"E83.MirrorCS"),sQuery(id+"F43.wireOp",EDGE,"E84.MirrorCS"),sQuery(id+"F43.wireOp",EDGE,"E85.MirrorCS"),sQuery(id+"F43.wireOp",EDGE,"E86.MirrorCS"),sQuery(id+"F43.wireOp",EDGE,"E88"),sQuery(id+"F43.wireOp",EDGE,"E89")])],"isStart":true});
            var sketch = newSketch(context, id + "F45", { "sketchPlane" : qUnion([Q0])});
            skLineSegment(sketch, "E90", {"start": v(-332.42, 284.65) * mm, "end": v(-270.8, 284.65) * mm});
            skEllipse(sketch, "E91", {"center": v(-270.8, 284.65) * mm, "majorRadius": 75.75 * mm, "minorRadius": 37.63 * mm, "majorAxis": v(0, 1)});
            skSolve(sketch);
        }
        {
            var Q0;
            Q0=makeQuery(id+"F45.imprint","IMPRINT",FACE,{"disambiguationData":[TD([[makeQuery(id+"F45.imprint","IMPRINT",EDGE,{"derivedFrom":sQuery(id+"F45.wireOp",EDGE,"E91")}),1.0]])]});
            extrude(context, id + "F46", {"entities" : qUnion([Q0]), "operationType" : NewBodyOperationType.REMOVE, "oppositeDirection" : true, "depth" : 25.4 * mm});
        }
        {
            var Q0;
            Q0=makeQuery(id+"F46.boolean.opBoolean","COPY",FACE,{"derivedFrom":makeQuery(id+"F46.opExtrude","CAP_FACE",FACE,{"disambiguationData":[OSD([sQuery(id+"F45.wireOp",EDGE,"E91")])],"isStart":false})});
            var Q1;
            Q1=makeQuery(id+"Fuy4HIbcask2fnl_9.1.F46.boolean.opBoolean","COPY",FACE,{"derivedFrom":makeQuery(id+"Fuy4HIbcask2fnl_9.1.F46.opExtrude","CAP_FACE",FACE,{"disambiguationData":[OSD([sQuery(id+"F45.wireOp",EDGE,"E91")])],"isStart":false})});
            extrude(context, id + "F47", {"entities" : qUnion([Q0, Q1]), "depth" : 12.7 * mm});
        }
        {
            var Q0;
            Q0=qCreatedBy(makeId("Front.planeOp"),FACE);
            cPlane(context, id + "F48", {"entities" : qUnion([Q0]), "cplaneType" : CPlaneType.OFFSET, "offset" : 304.8 * mm, "oppositeDirection" : true, "width" : 152.4 * mm, "height" : 152.4 * mm});
        }
        {
            var Q0;
            Q0=qCreatedBy(id+"F48.planeOp",FACE);
            var sketch = newSketch(context, id + "F49", { "sketchPlane" : qUnion([Q0])});
            skLineSegment(sketch, "E92", {"start": v(0, 0) * mm, "end": v(0, 254) * mm, "construction": true});
            skSolve(sketch);
        }
        {
            var Q1;
            Q1=makeQuery(id+"F44.opExtrude","CAP_FACE",FACE,{"disambiguationData":[OSD([sQuery(id+"F43.wireOp",EDGE,"E76"),sQuery(id+"F43.wireOp",EDGE,"E77"),sQuery(id+"F43.wireOp",EDGE,"E78"),sQuery(id+"F43.wireOp",EDGE,"E79.filletArc"),sQuery(id+"F43.wireOp",EDGE,"E80.filletArc"),sQuery(id+"F43.wireOp",EDGE,"E81.filletArc"),sQuery(id+"F43.wireOp",EDGE,"E82.MirrorCS"),sQuery(id+"F43.wireOp",EDGE,"E83.MirrorCS"),sQuery(id+"F43.wireOp",EDGE,"E84.MirrorCS"),sQuery(id+"F43.wireOp",EDGE,"E85.MirrorCS"),sQuery(id+"F43.wireOp",EDGE,"E86.MirrorCS"),sQuery(id+"F43.wireOp",EDGE,"E88"),sQuery(id+"F43.wireOp",EDGE,"E89")])],"isStart":false});
            var Q2;
            Q2=sQuery(id+"F49.wireOp",VERTEX,"E92.end");
            loft(context, id + "F50", {"operationType" : NewBodyOperationType.ADD, "sheetProfilesArray" : [{ "sheetProfileEntities" : qUnion([Q1]) }, { "sheetProfileEntities" : qUnion([Q2]) }]});
        }
        {
            var Q0;
            Q0=qCreatedBy(makeId("Top.planeOp"),FACE);
            cPlane(context, id + "F51", {"entities" : qUnion([Q0]), "cplaneType" : CPlaneType.OFFSET, "offset" : 406.4 * mm, "width" : 152.4 * mm, "height" : 152.4 * mm});
        }
        {
            var Q0;
            Q0=qCreatedBy(id+"F51.planeOp",FACE);
            var sketch = newSketch(context, id + "F52", { "sketchPlane" : qUnion([Q0])});
            skLineSegment(sketch, "E93.bottom", {"start": v(31.09, 879.75) * mm, "end": v(-31.09, 879.75) * mm});
            skLineSegment(sketch, "E93.top", {"start": v(31.09, 1019.37) * mm, "end": v(-31.09, 1019.37) * mm});
            skLineSegment(sketch, "E93.left", {"start": v(31.09, 879.75) * mm, "end": v(31.09, 1019.37) * mm});
            skLineSegment(sketch, "E93.right", {"start": v(-31.09, 879.75) * mm, "end": v(-31.09, 1019.37) * mm});
            skPoint(sketch, "E93.middle", {"position": v(0, 949.56) * mm});
            skSolve(sketch);
        }
        {
            var Q0;
            Q0=qCreatedBy(makeId("Right.planeOp"),FACE);
            var sketch = newSketch(context, id + "F53", { "sketchPlane" : qUnion([Q0])});
            skFitSpline(sketch, "E94.0", {"points": [v(762, 317.5) * mm, v(762, 298.45) * mm, v(762, 279.4) * mm, v(762, 260.35) * mm]});
            skFitSpline(sketch, "E95.0", {"points": [v(762, 146.05) * mm, v(762, 127) * mm, v(762, 107.95) * mm, v(762, 88.9) * mm]});
            skLineSegment(sketch, "E96.0", {"start": v(879.75, 406.4) * mm, "end": v(1019.37, 406.4) * mm});
            skFitSpline(sketch, "E97", {"points": [v(762, 317.5) * mm, v(826.34, 338.55) * mm, v(879.75, 406.4) * mm], "startDerivative": vector(145.53, 25.31) * mm, "endDerivative": vector(91.07, 149.96) * mm});
            skFitSpline(sketch, "E98", {"points": [v(1019.37, 406.4) * mm, v(879.75, 215.8) * mm, v(762, 88.9) * mm], "startDerivative": vector(-260.16, -374.94) * mm, "endDerivative": vector(-254.44, -257.01) * mm});
            skSolve(sketch);
        }
        {
            var Q1;
            Q1=makeQuery(id+"F52.imprint","IMPRINT",FACE,{"disambiguationData":[TD([[makeQuery(id+"F52.imprint","IMPRINT",EDGE,{"derivedFrom":sQuery(id+"F52.wireOp",EDGE,"E93.bottom")}),-1.0]])]});
            var Q2;
            Q2=makeQuery(id+"F9.opLoft","CAP_FACE",FACE,{"disambiguationData":[OSD([makeQuery(id+"F7.imprint","IMPRINT",FACE,{"disambiguationData":[TD([[makeQuery(id+"F7.imprint","IMPRINT",EDGE,{"derivedFrom":sQuery(id+"F7.wireOp",EDGE,"E20")}),1.0]])]})])],"isStart":true});
            var Q3;
            Q3=sQuery(id+"F53.wireOp",EDGE,"E97");
            var Q4;
            Q4=sQuery(id+"F53.wireOp",EDGE,"E98");
            loft(context, id + "F54", {"operationType" : NewBodyOperationType.ADD, "addGuides" : true, "sheetProfilesArray" : [{ "sheetProfileEntities" : qUnion([Q1]) }, { "sheetProfileEntities" : qUnion([Q2]) }], "guidesArray" : [{ "guideEntities" : qUnion([Q3]), "guideDerivativeType" : LoftGuideDerivativeType.DEFAULT, "guideDerivativeMagnitude" : 1 }, { "guideEntities" : qUnion([Q4]), "guideDerivativeType" : LoftGuideDerivativeType.DEFAULT, "guideDerivativeMagnitude" : 1 }]});
        }
        {
            var Q0;
            Q0=makeQuery(id+"F54.opLoft","CAP_FACE",FACE,{"disambiguationData":[OSD([makeQuery(id+"F52.imprint","IMPRINT",FACE,{"disambiguationData":[TD([[makeQuery(id+"F52.imprint","IMPRINT",EDGE,{"derivedFrom":sQuery(id+"F52.wireOp",EDGE,"E93.bottom")}),-1.0]])]})])],"isStart":true});
            var Q1;
            Q1=makeQuery(id+"F18.opExtrude","SWEPT_FACE",FACE,{"disambiguationData":[OSD([sQuery(id+"F17.wireOp",EDGE,"E37")])]});
            extrude(context, id + "F55", {"entities" : qUnion([Q0]), "endBound" : BoundingType.UP_TO_SURFACE, "endBoundEntityFace" : qUnion([Q1]), "depth" : 25.4 * mm});
        }
    });
